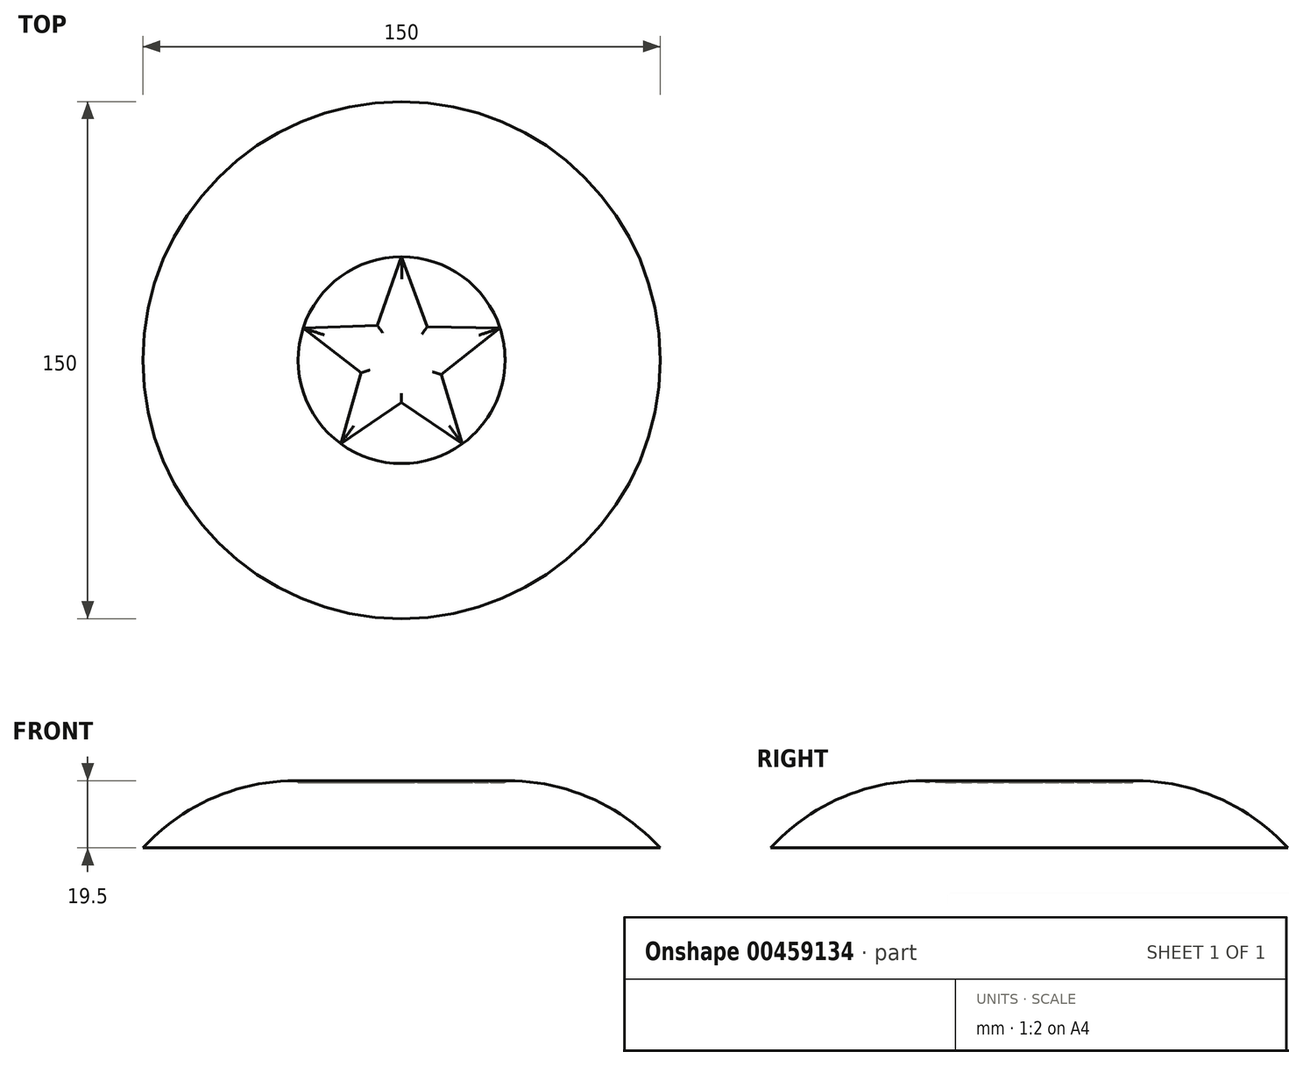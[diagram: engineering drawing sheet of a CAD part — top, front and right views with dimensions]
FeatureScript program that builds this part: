
annotation { "Feature Type Name" : "Feature", "Feature Type Description" : "" }
export const myFeature = defineFeature(function(context is Context, id is Id, definition is map)
    precondition{}
    {
        {
            var Q0;
            Q0=qCreatedBy(makeId("Top.planeOp"),FACE);
            var sketch = newSketch(context, id + "F0", { "sketchPlane" : qUnion([Q0])});
            skCircle(sketch, "E0", {"center": v(0, 0) * mm, "radius": 75 * mm});
            skCircle(sketch, "E1", {"center": v(0, 0) * mm, "radius": 60 * mm});
            skCircle(sketch, "E2", {"center": v(0, 0) * mm, "radius": 45 * mm});
            skCircle(sketch, "E3", {"center": v(0, 0) * mm, "radius": 30 * mm});
            skLineSegment(sketch, "E4", {"start": v(-28.53, 9.27) * mm, "end": v(-7.02, 10.03) * mm});
            skLineSegment(sketch, "E5", {"start": v(-7.02, 10.03) * mm, "end": v(0, 30) * mm});
            skLineSegment(sketch, "E6", {"start": v(0, 30) * mm, "end": v(7.45, 9.71) * mm});
            skLineSegment(sketch, "E7", {"start": v(7.45, 9.71) * mm, "end": v(28.53, 9.27) * mm});
            skLineSegment(sketch, "E8", {"start": v(28.53, 9.27) * mm, "end": v(11.5, -4.19) * mm});
            skLineSegment(sketch, "E9", {"start": v(11.5, -4.19) * mm, "end": v(17.63, -24.27) * mm});
            skLineSegment(sketch, "E10", {"start": v(17.63, -24.27) * mm, "end": v(0, -12.24) * mm});
            skLineSegment(sketch, "E11", {"start": v(0, -12.24) * mm, "end": v(-17.63, -24.27) * mm});
            skLineSegment(sketch, "E12", {"start": v(-17.63, -24.27) * mm, "end": v(-11.68, -3.68) * mm});
            skLineSegment(sketch, "E13", {"start": v(-11.68, -3.68) * mm, "end": v(-28.53, 9.27) * mm});
            skSolve(sketch);
        }
        {
            var Q0;
            Q0=makeQuery(id+"F0.imprint","IMPRINT",FACE,{"disambiguationData":[TD([[makeQuery(id+"F0.imprint","IMPRINT",EDGE,{"derivedFrom":sQuery(id+"F0.wireOp",EDGE,"E4")}),-1.0]])]});
            extrude(context, id + "F1", {"entities" : qUnion([Q0]), "depth" : 19.5 * mm});
        }
        {
            var Q0;
            {var subQ0=sQuery(id+"F0.wireOp",EDGE,"E6");Q0=makeQuery(id+"F0.imprint","IMPRINT",FACE,{"disambiguationData":[TD([[makeQuery(id+"F0.imprint","IMPRINT",EDGE,{"derivedFrom":subQ0}),1.0]])]});}
            var Q1;
            {var subQ0=sQuery(id+"F0.wireOp",EDGE,"E4");Q1=makeQuery(id+"F0.imprint","IMPRINT",FACE,{"disambiguationData":[TD([[makeQuery(id+"F0.imprint","IMPRINT",EDGE,{"derivedFrom":subQ0}),1.0]])]});}
            var Q2;
            {var subQ2=sQuery(id+"F0.wireOp",EDGE,"E12");Q2=makeQuery(id+"F0.imprint","IMPRINT",FACE,{"disambiguationData":[TD([[makeQuery(id+"F0.imprint","IMPRINT",EDGE,{"derivedFrom":subQ2}),1.0]])]});}
            var Q3;
            {var subQ0=sQuery(id+"F0.wireOp",EDGE,"E10");Q3=makeQuery(id+"F0.imprint","IMPRINT",FACE,{"disambiguationData":[TD([[makeQuery(id+"F0.imprint","IMPRINT",EDGE,{"derivedFrom":subQ0}),1.0]])]});}
            var Q4;
            {var subQ0=sQuery(id+"F0.wireOp",EDGE,"E8");Q4=makeQuery(id+"F0.imprint","IMPRINT",FACE,{"disambiguationData":[TD([[makeQuery(id+"F0.imprint","IMPRINT",EDGE,{"derivedFrom":subQ0}),1.0]])]});}
            extrude(context, id + "F2", {"entities" : qUnion([Q0, Q1, Q2, Q3, Q4]), "operationType" : NewBodyOperationType.ADD, "depth" : 19 * mm});
        }
        {
            var Q0;
            Q0=makeQuery(id+"F1.opExtrude","CAP_FACE",FACE,{"disambiguationData":[OSD([sQuery(id+"F0.wireOp",EDGE,"E4"),sQuery(id+"F0.wireOp",EDGE,"E5"),sQuery(id+"F0.wireOp",EDGE,"E6"),sQuery(id+"F0.wireOp",EDGE,"E7"),sQuery(id+"F0.wireOp",EDGE,"E8"),sQuery(id+"F0.wireOp",EDGE,"E9"),sQuery(id+"F0.wireOp",EDGE,"E10"),sQuery(id+"F0.wireOp",EDGE,"E11"),sQuery(id+"F0.wireOp",EDGE,"E12"),sQuery(id+"F0.wireOp",EDGE,"E13")])],"isStart":false});
            fillet(context, id + "F3", {"entities" : qUnion([Q0]), "radius" : 5 * mm, "tangentPropagation" : true, "allowEdgeOverflow" : false});
        }
        {
            var Q0;
            Q0=makeQuery(id+"F0.imprint","IMPRINT",FACE,{"disambiguationData":[TD([[makeQuery(id+"F0.imprint","IMPRINT",EDGE,{"derivedFrom":sQuery(id+"F0.wireOp",EDGE,"E2")}),1.0]])]});
            extrude(context, id + "F4", {"entities" : qUnion([Q0]), "operationType" : NewBodyOperationType.ADD, "depth" : 19.5 * mm});
        }
        {
            var Q0;
            Q0=makeQuery(id+"F4.opExtrude","CAP_EDGE",EDGE,{"disambiguationData":[OSD([sQuery(id+"F0.wireOp",EDGE,"E3")])],"isStart":false});
            fillet(context, id + "F5", {"entities" : qUnion([Q0]), "radius" : .5 * mm, "tangentPropagation" : true, "allowEdgeOverflow" : false});
        }
        {
            var Q0;
            Q0=makeQuery(id+"F0.imprint","IMPRINT",FACE,{"disambiguationData":[TD([[makeQuery(id+"F0.imprint","IMPRINT",EDGE,{"derivedFrom":sQuery(id+"F0.wireOp",EDGE,"E1")}),1.0]])]});
            var Q1;
            Q1=makeQuery(id+"F0.imprint","IMPRINT",FACE,{"disambiguationData":[TD([[makeQuery(id+"F0.imprint","IMPRINT",EDGE,{"derivedFrom":sQuery(id+"F0.wireOp",EDGE,"E0")}),1.0]])]});
            extrude(context, id + "F6", {"entities" : qUnion([Q0, Q1]), "operationType" : NewBodyOperationType.ADD, "depth" : 19.5 * mm});
        }
        {
            var Q0;
            {var subQ0=sQuery(id+"F0.wireOp",EDGE,"E2");Q0=makeQuery(id+"F6.boolean.opBoolean","MERGE",FACE,{"derivedFrom":[makeQuery(id+"F4.opExtrude","CAP_FACE",FACE,{"disambiguationData":[OSD([subQ0,sQuery(id+"F0.wireOp",EDGE,"E3")])],"isStart":false}),makeQuery(id+"F6.opExtrude","CAP_FACE",FACE,{"disambiguationData":[OSD([sQuery(id+"F0.wireOp",EDGE,"E0"),subQ0])],"isStart":false})]});}
            fillet(context, id + "F7", {"entities" : qUnion([Q0]), "radius" : 60 * mm, "tangentPropagation" : true, "allowEdgeOverflow" : false});
        }
        {
            var Q0;
            Q0=sQuery(id+"F0.wireOp",EDGE,"E1");
            extrude(context, id + "F8", {"bodyType" : ToolBodyType.SURFACE, "surfaceEntities" : qUnion([Q0]), "depth" : 12 * mm});
        }
        {
            var Q0;
            Q0=sQuery(id+"F0.wireOp",EDGE,"E2");
            extrude(context, id + "F9", {"bodyType" : ToolBodyType.SURFACE, "surfaceEntities" : qUnion([Q0]), "depth" : 18 * mm});
        }
    });
